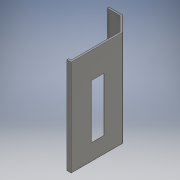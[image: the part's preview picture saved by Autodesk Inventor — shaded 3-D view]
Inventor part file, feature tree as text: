
AUTODESK INVENTOR PART (.ipt)
format: ipt  version: 2018 (Build 220112000, 112)  size: 179,712 bytes
history: native  units: mm
features: extrude x6, sketch x6, projected_geometry x1
ambient origin geometry x8: Origin, YZ Plane, XZ Plane, XY Plane, X Axis, Y Axis, Z Axis, Center Point
bodies: Solid1 (feature_tree)
feature tree (13):
  extrude  "Extrusion1"  TaperAngle=45.0deg  [1 undecoded]
  extrude  "Extrusion3"  Depth=50.0mm
  extrude  "Extrusion4"  Depth=195.0mm
  extrude  "Extrusion5"  Depth=650.0mm
  extrude  "Extrusion6"  Depth=150.0mm
  extrude  "Extrusion7"  Depth=1.6mm
  sketch  "Sketch1"  dims[d0=167.6mm d1=45.0deg]
  sketch  "Sketch2"  dims[d2=800.0mm d4=50.0mm]
  sketch  "Sketch3"  dims[d6=1160.0mm d7=0.0mm d8=195.0mm]
  sketch  "Sketch4"  dims[d10=650.0mm d11=650.0mm]
  projected_geometry  "Projected Loop1"
  sketch  "Sketch5"  dims[d12=150.0mm d15=180.0mm]
  sketch  "Sketch6"  dims[d19=1.6mm d20=320.0mm d21=10.0mm d22=0.0mm d23=20.0mm d24=1.6mm d25=0.0mm d26=1.6mm d27=0.0mm d28=1.6mm d29=0.0mm d30=1.6mm d31=1.6mm d32=1.6mm d33=0.0mm]
note: 1 required parameter value undecoded (feature->parameter linkage not recoverable at this tier; creation-order binding heuristic only, values carry confidence <= 0.55)
